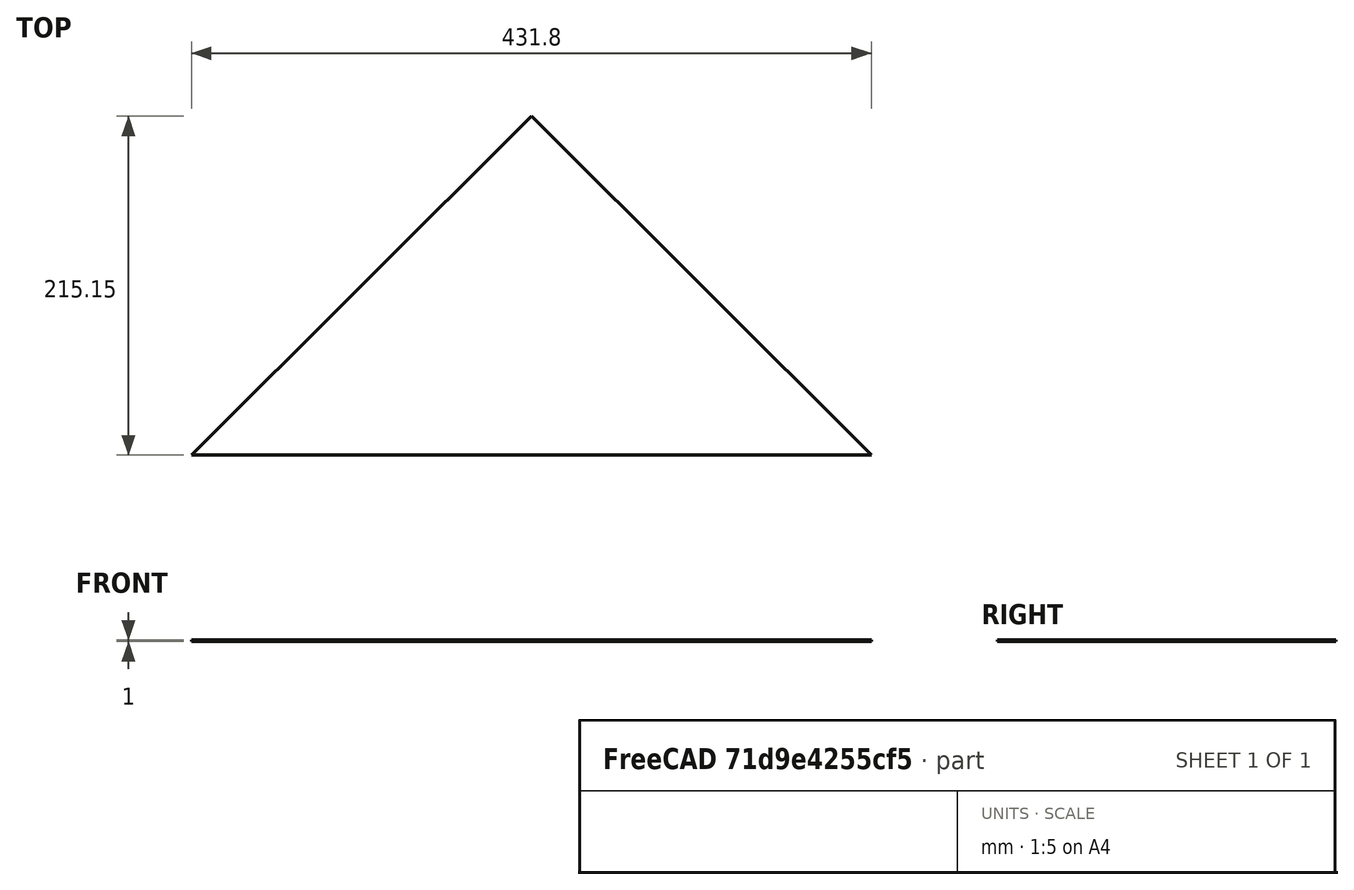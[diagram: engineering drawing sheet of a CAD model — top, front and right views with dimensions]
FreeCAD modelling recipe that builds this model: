
FCSTD DOCUMENT  (FreeCAD 0.19R22411 (Git))
Label: ala
License: All rights reserved
LicenseURL: http://en.wikipedia.org/wiki/All_rights_reserved
objects: Sketcher::SketchObject×1, PartDesign::Pad×1, PartDesign::Body×1
note: 4 computed .brp shape members not serialized (recipe doc carries the construction recipe); baked Part::Feature solids carry a one-line shape summary decoded from their .brp

FEATURE [Sketcher::SketchObject] Sketch
  sketch-geometry (4):
    g0: LineSegment StartX=-215.9 StartY=0 StartZ=0 EndX=-2.84e-14 EndY=215.152 EndZ=0
    g1: LineSegment StartX=-2.12e-14 StartY=215.152 StartZ=0 EndX=215.9 EndY=-2.84e-14 EndZ=0
    g2: LineSegment StartX=-215.9 StartY=0 StartZ=0 EndX=0 EndY=0 EndZ=0
    g3: LineSegment StartX=0 StartY=0 StartZ=0 EndX=215.9 EndY=0 EndZ=0
  constraints (11):
    c: Coincident(g1,g0)
    c: Coincident(g3,g1)
    c: Coincident(g2,g3)
    c: Horizontal(g2)
    c: Horizontal(g3)
    c: Equal(g2,g3)
    c: Coincident(g2,g0)
    c: Coincident(g2,g-1)
    c: Equal(g0,g1)
    c: Distance(g0,g1) = 304.8
    c: DistanceX(g0,g1) = 431.8
FEATURE [PartDesign::Pad] Pad
  AllowMultiFace = false
  Length = 1
  Length2 = 100
  Profile = -> Sketch
  Type = 0
FEATURE [PartDesign::Body] Body
  Group = -> [Sketch,Pad]
  Origin = -> Origin
  Tip = -> Pad
